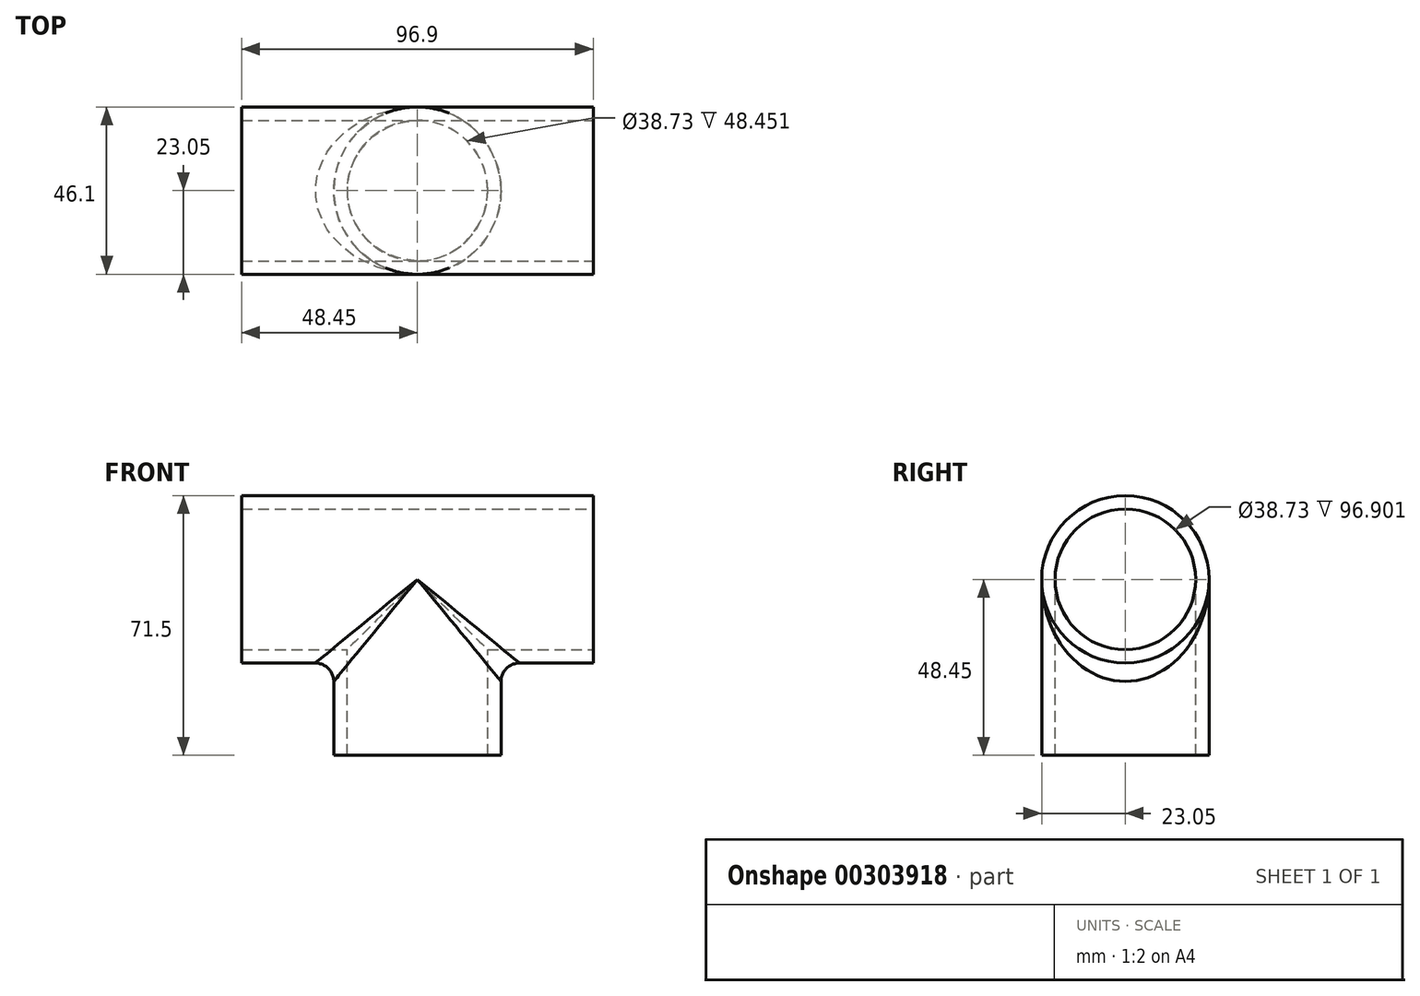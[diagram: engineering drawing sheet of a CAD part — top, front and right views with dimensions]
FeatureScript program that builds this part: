
annotation { "Feature Type Name" : "Feature", "Feature Type Description" : "" }
export const myFeature = defineFeature(function(context is Context, id is Id, definition is map)
    precondition{}
    {
        {
            var Q0;
            Q0=qCreatedBy(makeId("Front.planeOp"),FACE);
            var sketch = newSketch(context, id + "F0", { "sketchPlane" : qUnion([Q0])});
            skLineSegment(sketch, "E0", {"start": v(0, 0) * mm, "end": v(-48.45, 0) * mm});
            skLineSegment(sketch, "E1", {"start": v(-48.45, 0) * mm, "end": v(-48.45, -23.05) * mm});
            skLineSegment(sketch, "E2", {"start": v(0, 0) * mm, "end": v(48.45, 0) * mm});
            skLineSegment(sketch, "E3", {"start": v(48.45, 0) * mm, "end": v(48.45, -23.05) * mm});
            skLineSegment(sketch, "E4", {"start": v(48.45, -23.05) * mm, "end": v(23.05, -23.05) * mm, "construction": true});
            skLineSegment(sketch, "E5", {"start": v(23.05, -23.05) * mm, "end": v(23.05, -48.45) * mm, "construction": true});
            skLineSegment(sketch, "E6", {"start": v(23.05, -48.45) * mm, "end": v(0, -48.45) * mm});
            skLineSegment(sketch, "E7", {"start": v(0, -48.45) * mm, "end": v(0, -23.05) * mm});
            skLineSegment(sketch, "E8", {"start": v(0, -23.05) * mm, "end": v(23.05, -23.05) * mm});
            skLineSegment(sketch, "E9", {"start": v(0, -48.45) * mm, "end": v(-23.05, -48.45) * mm});
            skLineSegment(sketch, "E10", {"start": v(-23.05, -48.45) * mm, "end": v(-23.05, -23.05) * mm, "construction": true});
            skLineSegment(sketch, "E11", {"start": v(-23.05, -23.05) * mm, "end": v(0, -23.05) * mm});
            skLineSegment(sketch, "E12", {"start": v(0, 0) * mm, "end": v(0, -23.05) * mm});
            skLineSegment(sketch, "E13", {"start": v(-48.45, 0) * mm, "end": v(-48.45, 23.05) * mm});
            skLineSegment(sketch, "E14", {"start": v(-48.45, 23.05) * mm, "end": v(48.45, 23.05) * mm, "construction": true});
            skLineSegment(sketch, "E15", {"start": v(48.45, 23.05) * mm, "end": v(48.45, 0) * mm});
            skLineSegment(sketch, "E16", {"start": v(-48.45, -23.05) * mm, "end": v(-23.05, -23.05) * mm, "construction": true});
            skSolve(sketch);
        }
        {
            var Q0;
            Q0=sQuery(id+"F0.wireOp",EDGE,"E14");
            var Q1;
            Q1=sQuery(id+"F0.wireOp",EDGE,"E16");
            var Q2;
            Q2=sQuery(id+"F0.wireOp",EDGE,"E4");
            var Q3;
            Q3=sQuery(id+"F0.wireOp",EDGE,"E10");
            var Q4;
            Q4=sQuery(id+"F0.wireOp",EDGE,"E13");
            var Q5;
            Q5=sQuery(id+"F0.wireOp",EDGE,"E0");
            revolve(context, id + "F1", {"bodyType" : ToolBodyType.SURFACE, "surfaceEntities" : qUnion([Q0, Q1, Q2, Q3, Q4]), "axis" : qUnion([Q5]), "revolveType" : RevolveType.FULL});
        }
        {
            var Q0;
            Q0=sQuery(id+"F0.wireOp",EDGE,"E9");
            var Q1;
            Q1=sQuery(id+"F0.wireOp",EDGE,"E7");
            revolve(context, id + "F2", {"bodyType" : ToolBodyType.SURFACE, "surfaceEntities" : qUnion([Q0]), "axis" : qUnion([Q1]), "revolveType" : RevolveType.FULL});
        }
        {
            var Q0;
            Q0=sQuery(id+"F0.wireOp",EDGE,"E15");
            var Q1;
            Q1=sQuery(id+"F0.wireOp",EDGE,"E2");
            revolve(context, id + "F3", {"bodyType" : ToolBodyType.SURFACE, "surfaceEntities" : qUnion([Q0]), "axis" : qUnion([Q1]), "revolveType" : RevolveType.FULL});
        }
        {
            var Q0;
            Q0=makeQuery(id+"F1.opRevolve","SWEPT_FACE",FACE,{"disambiguationData":[OSD([sQuery(id+"F0.wireOp",EDGE,"E13")])]});
            var Q1;
            Q1=sQuery(id+"F0.wireOp",EDGE,"E0");
            var Q2;
            Q2=sQuery(id+"F0.wireOp",EDGE,"E2");
            sweep(context, id + "F4", {"profiles" : qUnion([Q0]), "path" : qUnion([Q1, Q2])});
        }
        {
            var Q0;
            Q0=makeQuery(id+"F2.opRevolve","SWEPT_FACE",FACE,{"disambiguationData":[OSD([sQuery(id+"F0.wireOp",EDGE,"E9")])]});
            var Q1;
            Q1=sQuery(id+"F0.wireOp",EDGE,"E12");
            var Q2;
            Q2=sQuery(id+"F0.wireOp",EDGE,"E7");
            sweep(context, id + "F5", {"operationType" : NewBodyOperationType.ADD, "profiles" : qUnion([Q0]), "path" : qUnion([Q1, Q2])});
        }
        {
            var Q0;
            Q0=makeQuery(id+"F4.opSweep","CAP_FACE",FACE,{"disambiguationData":[OSD([sQuery(id+"F0.wireOp",VERTEX,"E2.end"),sQuery(id+"F0.wireOp",EDGE,"E13")])],"isStart":false});
            var Q1;
            Q1=makeQuery(id+"F4.opSweep","CAP_FACE",FACE,{"disambiguationData":[OSD([sQuery(id+"F0.wireOp",VERTEX,"E0.end"),sQuery(id+"F0.wireOp",EDGE,"E13")])],"isStart":true});
            var Q2;
            Q2=makeQuery(id+"F5.opSweep","CAP_FACE",FACE,{"disambiguationData":[OSD([sQuery(id+"F0.wireOp",VERTEX,"E7.start"),sQuery(id+"F0.wireOp",EDGE,"E9")])],"isStart":true});
            shell(context, id + "F6", {"entities" : qUnion([Q0, Q1, Q2]), "thickness" : 3.68 * mm});
        }
        {
            var Q0;
            Q0=makeQuery(id+"F5.boolean.opBoolean","INTERSECT",EDGE,{"disambiguationData":[OD(0.0)],"derivedFrom":[makeQuery(id+"F4.opSweep","SWEPT_FACE",FACE,{"disambiguationData":[OSD([sQuery(id+"F0.wireOp",VERTEX,"E13.end"),sQuery(id+"F0.wireOp",EDGE,"E0")])]}),makeQuery(id+"F5.opSweep","SWEPT_FACE",FACE,{"disambiguationData":[OSD([sQuery(id+"F0.wireOp",VERTEX,"E9.end"),sQuery(id+"F0.wireOp",EDGE,"E7")])]})]});
            var Q1;
            Q1=makeQuery(id+"F5.boolean.opBoolean","INTERSECT",EDGE,{"disambiguationData":[OD(1.0)],"derivedFrom":[makeQuery(id+"F4.opSweep","SWEPT_FACE",FACE,{"disambiguationData":[OSD([sQuery(id+"F0.wireOp",VERTEX,"E13.end"),sQuery(id+"F0.wireOp",EDGE,"E0")])]}),makeQuery(id+"F5.opSweep","SWEPT_FACE",FACE,{"disambiguationData":[OSD([sQuery(id+"F0.wireOp",VERTEX,"E9.end"),sQuery(id+"F0.wireOp",EDGE,"E7")])]})]});
            fillet(context, id + "F7", {"entities" : qUnion([Q0, Q1]), "radius" : 5.08 * mm, "tangentPropagation" : true, "allowEdgeOverflow" : false});
        }
    });
